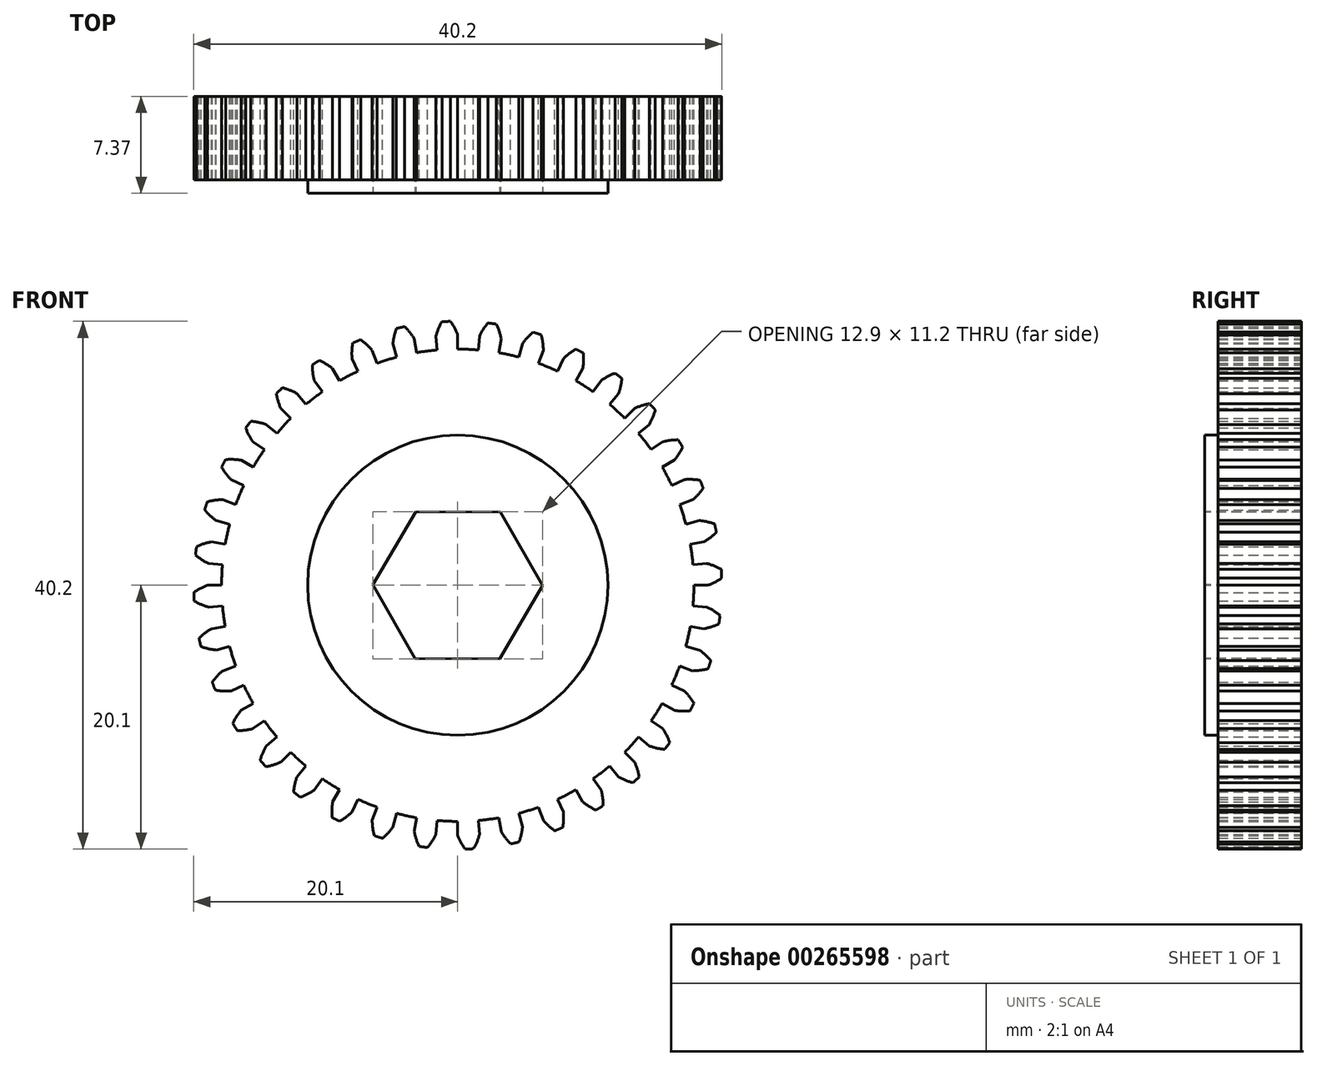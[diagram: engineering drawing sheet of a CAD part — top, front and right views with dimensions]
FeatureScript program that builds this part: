
annotation { "Feature Type Name" : "Feature", "Feature Type Description" : "" }
export const myFeature = defineFeature(function(context is Context, id is Id, definition is map)
    precondition{}
    {
        {
            var Q0;
            Q0=qCreatedBy(makeId("Front.planeOp"),FACE);
            var sketch = newSketch(context, id + "F0", { "sketchPlane" : qUnion([Q0])});
            skArc(sketch, "E0", {"start": v(-1.57, 17.91) * mm, "mid": v(-2.35, 17.83) * mm, "end": v(-3.12, 17.7) * mm});
            skArc(sketch, "E1", {"start": v(-0.55, 20.1) * mm, "mid": v(-0.71, 20.1) * mm, "end": v(-0.88, 20.08) * mm});
            skPoint(sketch, "E2.endSnap0", {"position": v(-1.68, 19.21) * mm});
            skArc(sketch, "E3.trimOffspring", {"start": v(0, 19.05) * mm, "mid": v(-0.24, 19.6) * mm, "end": v(-0.55, 20.1) * mm});
            skLineSegment(sketch, "E4.trimOffspring", {"start": v(0, 17.93) * mm, "end": v(0, 19.05) * mm});
            skLineSegment(sketch, "E5.MirrorCS", {"start": v(-1.56, 17.86) * mm, "end": v(-1.66, 18.98) * mm});
            skArc(sketch, "E6.MirrorCS", {"start": v(-1.66, 18.98) * mm, "mid": v(-1.47, 19.54) * mm, "end": v(-1.2, 20.07) * mm});
            skArc(sketch, "E7.MirrorCS", {"start": v(-1.2, 20.07) * mm, "mid": v(-1.04, 20.08) * mm, "end": v(-0.88, 20.08) * mm});
            skArc(sketch, "E8.1.0", {"start": v(-4.67, 19.55) * mm, "mid": v(-4.51, 19.6) * mm, "end": v(-4.35, 19.63) * mm});
            skArc(sketch, "E8.1.1", {"start": v(-4.93, 18.4) * mm, "mid": v(-4.84, 18.99) * mm, "end": v(-4.67, 19.55) * mm});
            skLineSegment(sketch, "E8.1.2", {"start": v(-4.64, 17.32) * mm, "end": v(-4.93, 18.4) * mm});
            skArc(sketch, "E8.1.3", {"start": v(-4.03, 19.7) * mm, "mid": v(-4.2, 19.66) * mm, "end": v(-4.35, 19.63) * mm});
            skArc(sketch, "E8.1.4", {"start": v(-3.3, 18.76) * mm, "mid": v(-3.64, 19.25) * mm, "end": v(-4.03, 19.7) * mm});
            skLineSegment(sketch, "E8.1.5", {"start": v(-3.11, 17.66) * mm, "end": v(-3.3, 18.76) * mm});
            skArc(sketch, "E8.2.0", {"start": v(-8, 18.45) * mm, "mid": v(-7.84, 18.51) * mm, "end": v(-7.7, 18.57) * mm});
            skArc(sketch, "E8.2.1", {"start": v(-8.05, 17.27) * mm, "mid": v(-8.06, 17.86) * mm, "end": v(-8, 18.45) * mm});
            skLineSegment(sketch, "E8.2.2", {"start": v(-7.58, 16.25) * mm, "end": v(-8.05, 17.27) * mm});
            skArc(sketch, "E8.2.3", {"start": v(-7.4, 18.7) * mm, "mid": v(-7.54, 18.64) * mm, "end": v(-7.7, 18.57) * mm});
            skArc(sketch, "E8.2.4", {"start": v(-6.52, 17.9) * mm, "mid": v(-6.93, 18.33) * mm, "end": v(-7.4, 18.7) * mm});
            skLineSegment(sketch, "E8.2.5", {"start": v(-6.13, 16.85) * mm, "end": v(-6.52, 17.9) * mm});
            skArc(sketch, "E8.3.0", {"start": v(-11.08, 16.78) * mm, "mid": v(-10.94, 16.87) * mm, "end": v(-10.8, 16.96) * mm});
            skArc(sketch, "E8.3.1", {"start": v(-10.93, 15.6) * mm, "mid": v(-11.04, 16.19) * mm, "end": v(-11.08, 16.78) * mm});
            skLineSegment(sketch, "E8.3.2", {"start": v(-10.29, 14.69) * mm, "end": v(-10.93, 15.6) * mm});
            skArc(sketch, "E8.3.3", {"start": v(-10.53, 17.13) * mm, "mid": v(-10.66, 17.04) * mm, "end": v(-10.8, 16.96) * mm});
            skArc(sketch, "E8.3.4", {"start": v(-9.52, 16.5) * mm, "mid": v(-10, 16.84) * mm, "end": v(-10.53, 17.13) * mm});
            skLineSegment(sketch, "E8.3.5", {"start": v(-8.97, 15.53) * mm, "end": v(-9.52, 16.5) * mm});
            skArc(sketch, "E8.4.0", {"start": v(-13.82, 14.6) * mm, "mid": v(-13.7, 14.71) * mm, "end": v(-13.58, 14.82) * mm});
            skArc(sketch, "E8.4.1", {"start": v(-13.47, 13.47) * mm, "mid": v(-13.68, 14.02) * mm, "end": v(-13.82, 14.6) * mm});
            skLineSegment(sketch, "E8.4.2", {"start": v(-12.68, 12.68) * mm, "end": v(-13.47, 13.47) * mm});
            skArc(sketch, "E8.4.3", {"start": v(-13.34, 15.04) * mm, "mid": v(-13.46, 14.93) * mm, "end": v(-13.58, 14.82) * mm});
            skArc(sketch, "E8.4.4", {"start": v(-12.25, 14.6) * mm, "mid": v(-12.78, 14.85) * mm, "end": v(-13.34, 15.04) * mm});
            skLineSegment(sketch, "E8.4.5", {"start": v(-11.53, 13.74) * mm, "end": v(-12.25, 14.6) * mm});
            skArc(sketch, "E8.5.0", {"start": v(-16.15, 11.98) * mm, "mid": v(-16.05, 12.1) * mm, "end": v(-15.95, 12.24) * mm});
            skArc(sketch, "E8.5.1", {"start": v(-15.6, 10.93) * mm, "mid": v(-15.9, 11.44) * mm, "end": v(-16.15, 11.98) * mm});
            skLineSegment(sketch, "E8.5.2", {"start": v(-14.69, 10.29) * mm, "end": v(-15.6, 10.93) * mm});
            skArc(sketch, "E8.5.3", {"start": v(-15.75, 12.5) * mm, "mid": v(-15.85, 12.37) * mm, "end": v(-15.95, 12.24) * mm});
            skArc(sketch, "E8.5.4", {"start": v(-14.6, 12.25) * mm, "mid": v(-15.16, 12.4) * mm, "end": v(-15.75, 12.5) * mm});
            skLineSegment(sketch, "E8.5.5", {"start": v(-13.74, 11.53) * mm, "end": v(-14.6, 12.25) * mm});
            skArc(sketch, "E8.6.0", {"start": v(-17.98, 9) * mm, "mid": v(-17.9, 9.14) * mm, "end": v(-17.83, 9.28) * mm});
            skArc(sketch, "E8.6.1", {"start": v(-17.27, 8.05) * mm, "mid": v(-17.65, 8.5) * mm, "end": v(-17.98, 9) * mm});
            skLineSegment(sketch, "E8.6.2", {"start": v(-16.25, 7.58) * mm, "end": v(-17.27, 8.05) * mm});
            skArc(sketch, "E8.6.3", {"start": v(-17.68, 9.57) * mm, "mid": v(-17.76, 9.43) * mm, "end": v(-17.83, 9.28) * mm});
            skArc(sketch, "E8.6.4", {"start": v(-16.5, 9.53) * mm, "mid": v(-17.09, 9.58) * mm, "end": v(-17.68, 9.57) * mm});
            skLineSegment(sketch, "E8.6.5", {"start": v(-15.53, 8.97) * mm, "end": v(-16.5, 9.53) * mm});
            skArc(sketch, "E8.7.0", {"start": v(-19.27, 5.73) * mm, "mid": v(-19.22, 5.89) * mm, "end": v(-19.17, 6.05) * mm});
            skArc(sketch, "E8.7.1", {"start": v(-18.4, 4.93) * mm, "mid": v(-18.86, 5.3) * mm, "end": v(-19.27, 5.73) * mm});
            skLineSegment(sketch, "E8.7.2", {"start": v(-17.32, 4.64) * mm, "end": v(-18.4, 4.93) * mm});
            skArc(sketch, "E8.7.3", {"start": v(-19.07, 6.36) * mm, "mid": v(-19.12, 6.2) * mm, "end": v(-19.17, 6.05) * mm});
            skArc(sketch, "E8.7.4", {"start": v(-17.9, 6.52) * mm, "mid": v(-18.5, 6.47) * mm, "end": v(-19.07, 6.36) * mm});
            skLineSegment(sketch, "E8.7.5", {"start": v(-16.85, 6.13) * mm, "end": v(-17.9, 6.52) * mm});
            skArc(sketch, "E8.8.0", {"start": v(-19.97, 2.3) * mm, "mid": v(-19.95, 2.46) * mm, "end": v(-19.93, 2.62) * mm});
            skArc(sketch, "E8.8.1", {"start": v(-18.98, 1.66) * mm, "mid": v(-19.5, 1.95) * mm, "end": v(-19.97, 2.3) * mm});
            skLineSegment(sketch, "E8.8.2", {"start": v(-17.86, 1.56) * mm, "end": v(-18.98, 1.66) * mm});
            skArc(sketch, "E8.8.3", {"start": v(-19.89, 2.95) * mm, "mid": v(-19.91, 2.79) * mm, "end": v(-19.93, 2.62) * mm});
            skArc(sketch, "E8.8.4", {"start": v(-18.76, 3.3) * mm, "mid": v(-19.34, 3.16) * mm, "end": v(-19.89, 2.95) * mm});
            skLineSegment(sketch, "E8.8.5", {"start": v(-17.66, 3.11) * mm, "end": v(-18.76, 3.3) * mm});
            skArc(sketch, "E8.9.0", {"start": v(-20.07, -1.2) * mm, "mid": v(-20.08, -1.04) * mm, "end": v(-20.08, -0.88) * mm});
            skArc(sketch, "E8.9.1", {"start": v(-18.98, -1.66) * mm, "mid": v(-19.54, -1.47) * mm, "end": v(-20.07, -1.2) * mm});
            skLineSegment(sketch, "E8.9.2", {"start": v(-17.86, -1.56) * mm, "end": v(-18.98, -1.66) * mm});
            skArc(sketch, "E8.9.3", {"start": v(-20.1, -0.55) * mm, "mid": v(-20.1, -0.71) * mm, "end": v(-20.08, -0.88) * mm});
            skArc(sketch, "E8.9.4", {"start": v(-19.05, 0) * mm, "mid": v(-19.6, -0.24) * mm, "end": v(-20.1, -0.55) * mm});
            skLineSegment(sketch, "E8.9.5", {"start": v(-17.93, 0) * mm, "end": v(-19.05, 0) * mm});
            skArc(sketch, "E8.10.0", {"start": v(-19.55, -4.67) * mm, "mid": v(-19.6, -4.51) * mm, "end": v(-19.63, -4.35) * mm});
            skArc(sketch, "E8.10.1", {"start": v(-18.4, -4.93) * mm, "mid": v(-18.99, -4.84) * mm, "end": v(-19.55, -4.67) * mm});
            skLineSegment(sketch, "E8.10.2", {"start": v(-17.32, -4.64) * mm, "end": v(-18.4, -4.93) * mm});
            skArc(sketch, "E8.10.3", {"start": v(-19.7, -4.03) * mm, "mid": v(-19.66, -4.2) * mm, "end": v(-19.63, -4.35) * mm});
            skArc(sketch, "E8.10.4", {"start": v(-18.76, -3.3) * mm, "mid": v(-19.25, -3.64) * mm, "end": v(-19.7, -4.03) * mm});
            skLineSegment(sketch, "E8.10.5", {"start": v(-17.66, -3.11) * mm, "end": v(-18.76, -3.3) * mm});
            skArc(sketch, "E8.11.0", {"start": v(-18.45, -8) * mm, "mid": v(-18.51, -7.84) * mm, "end": v(-18.57, -7.7) * mm});
            skArc(sketch, "E8.11.1", {"start": v(-17.27, -8.05) * mm, "mid": v(-17.86, -8.06) * mm, "end": v(-18.45, -8) * mm});
            skLineSegment(sketch, "E8.11.2", {"start": v(-16.25, -7.58) * mm, "end": v(-17.27, -8.05) * mm});
            skArc(sketch, "E8.11.3", {"start": v(-18.7, -7.4) * mm, "mid": v(-18.64, -7.54) * mm, "end": v(-18.57, -7.7) * mm});
            skArc(sketch, "E8.11.4", {"start": v(-17.9, -6.52) * mm, "mid": v(-18.33, -6.93) * mm, "end": v(-18.7, -7.4) * mm});
            skLineSegment(sketch, "E8.11.5", {"start": v(-16.85, -6.13) * mm, "end": v(-17.9, -6.52) * mm});
            skArc(sketch, "E8.12.0", {"start": v(-16.78, -11.08) * mm, "mid": v(-16.87, -10.94) * mm, "end": v(-16.96, -10.8) * mm});
            skArc(sketch, "E8.12.1", {"start": v(-15.6, -10.93) * mm, "mid": v(-16.19, -11.04) * mm, "end": v(-16.78, -11.08) * mm});
            skLineSegment(sketch, "E8.12.2", {"start": v(-14.69, -10.29) * mm, "end": v(-15.6, -10.93) * mm});
            skArc(sketch, "E8.12.3", {"start": v(-17.13, -10.53) * mm, "mid": v(-17.04, -10.66) * mm, "end": v(-16.96, -10.8) * mm});
            skArc(sketch, "E8.12.4", {"start": v(-16.5, -9.52) * mm, "mid": v(-16.84, -10) * mm, "end": v(-17.13, -10.53) * mm});
            skLineSegment(sketch, "E8.12.5", {"start": v(-15.53, -8.97) * mm, "end": v(-16.5, -9.52) * mm});
            skArc(sketch, "E8.13.0", {"start": v(-14.6, -13.82) * mm, "mid": v(-14.71, -13.7) * mm, "end": v(-14.82, -13.58) * mm});
            skArc(sketch, "E8.13.1", {"start": v(-13.47, -13.47) * mm, "mid": v(-14.02, -13.68) * mm, "end": v(-14.6, -13.82) * mm});
            skLineSegment(sketch, "E8.13.2", {"start": v(-12.68, -12.68) * mm, "end": v(-13.47, -13.47) * mm});
            skArc(sketch, "E8.13.3", {"start": v(-15.04, -13.34) * mm, "mid": v(-14.93, -13.46) * mm, "end": v(-14.82, -13.58) * mm});
            skArc(sketch, "E8.13.4", {"start": v(-14.6, -12.25) * mm, "mid": v(-14.85, -12.78) * mm, "end": v(-15.04, -13.34) * mm});
            skLineSegment(sketch, "E8.13.5", {"start": v(-13.74, -11.53) * mm, "end": v(-14.6, -12.25) * mm});
            skArc(sketch, "E8.14.0", {"start": v(-11.98, -16.15) * mm, "mid": v(-12.1, -16.05) * mm, "end": v(-12.24, -15.95) * mm});
            skArc(sketch, "E8.14.1", {"start": v(-10.93, -15.6) * mm, "mid": v(-11.44, -15.9) * mm, "end": v(-11.98, -16.15) * mm});
            skLineSegment(sketch, "E8.14.2", {"start": v(-10.29, -14.69) * mm, "end": v(-10.93, -15.6) * mm});
            skArc(sketch, "E8.14.3", {"start": v(-12.5, -15.75) * mm, "mid": v(-12.37, -15.85) * mm, "end": v(-12.24, -15.95) * mm});
            skArc(sketch, "E8.14.4", {"start": v(-12.25, -14.6) * mm, "mid": v(-12.4, -15.16) * mm, "end": v(-12.5, -15.75) * mm});
            skLineSegment(sketch, "E8.14.5", {"start": v(-11.53, -13.74) * mm, "end": v(-12.25, -14.6) * mm});
            skArc(sketch, "E8.15.0", {"start": v(-9, -17.98) * mm, "mid": v(-9.14, -17.9) * mm, "end": v(-9.28, -17.83) * mm});
            skArc(sketch, "E8.15.1", {"start": v(-8.05, -17.27) * mm, "mid": v(-8.5, -17.65) * mm, "end": v(-9, -17.98) * mm});
            skLineSegment(sketch, "E8.15.2", {"start": v(-7.58, -16.25) * mm, "end": v(-8.05, -17.27) * mm});
            skArc(sketch, "E8.15.3", {"start": v(-9.57, -17.68) * mm, "mid": v(-9.43, -17.76) * mm, "end": v(-9.28, -17.83) * mm});
            skArc(sketch, "E8.15.4", {"start": v(-9.53, -16.5) * mm, "mid": v(-9.58, -17.09) * mm, "end": v(-9.57, -17.68) * mm});
            skLineSegment(sketch, "E8.15.5", {"start": v(-8.97, -15.53) * mm, "end": v(-9.53, -16.5) * mm});
            skArc(sketch, "E8.16.0", {"start": v(-5.73, -19.27) * mm, "mid": v(-5.89, -19.22) * mm, "end": v(-6.05, -19.17) * mm});
            skArc(sketch, "E8.16.1", {"start": v(-4.93, -18.4) * mm, "mid": v(-5.3, -18.86) * mm, "end": v(-5.73, -19.27) * mm});
            skLineSegment(sketch, "E8.16.2", {"start": v(-4.64, -17.32) * mm, "end": v(-4.93, -18.4) * mm});
            skArc(sketch, "E8.16.3", {"start": v(-6.36, -19.07) * mm, "mid": v(-6.2, -19.12) * mm, "end": v(-6.05, -19.17) * mm});
            skArc(sketch, "E8.16.4", {"start": v(-6.52, -17.9) * mm, "mid": v(-6.47, -18.5) * mm, "end": v(-6.36, -19.07) * mm});
            skLineSegment(sketch, "E8.16.5", {"start": v(-6.13, -16.85) * mm, "end": v(-6.52, -17.9) * mm});
            skArc(sketch, "E8.17.0", {"start": v(-2.3, -19.97) * mm, "mid": v(-2.46, -19.95) * mm, "end": v(-2.62, -19.93) * mm});
            skArc(sketch, "E8.17.1", {"start": v(-1.66, -18.98) * mm, "mid": v(-1.95, -19.5) * mm, "end": v(-2.3, -19.97) * mm});
            skLineSegment(sketch, "E8.17.2", {"start": v(-1.56, -17.86) * mm, "end": v(-1.66, -18.98) * mm});
            skArc(sketch, "E8.17.3", {"start": v(-2.95, -19.89) * mm, "mid": v(-2.79, -19.91) * mm, "end": v(-2.62, -19.93) * mm});
            skArc(sketch, "E8.17.4", {"start": v(-3.3, -18.76) * mm, "mid": v(-3.16, -19.34) * mm, "end": v(-2.95, -19.89) * mm});
            skLineSegment(sketch, "E8.17.5", {"start": v(-3.11, -17.66) * mm, "end": v(-3.3, -18.76) * mm});
            skArc(sketch, "E8.18.0", {"start": v(1.2, -20.07) * mm, "mid": v(1.04, -20.08) * mm, "end": v(0.88, -20.08) * mm});
            skArc(sketch, "E8.18.1", {"start": v(1.66, -18.98) * mm, "mid": v(1.47, -19.54) * mm, "end": v(1.2, -20.07) * mm});
            skLineSegment(sketch, "E8.18.2", {"start": v(1.56, -17.86) * mm, "end": v(1.66, -18.98) * mm});
            skArc(sketch, "E8.18.3", {"start": v(0.55, -20.1) * mm, "mid": v(0.71, -20.1) * mm, "end": v(0.88, -20.08) * mm});
            skArc(sketch, "E8.18.4", {"start": v(0, -19.05) * mm, "mid": v(0.24, -19.6) * mm, "end": v(0.55, -20.1) * mm});
            skLineSegment(sketch, "E8.18.5", {"start": v(0, -17.93) * mm, "end": v(0, -19.05) * mm});
            skArc(sketch, "E8.19.0", {"start": v(4.67, -19.55) * mm, "mid": v(4.51, -19.6) * mm, "end": v(4.35, -19.63) * mm});
            skArc(sketch, "E8.19.1", {"start": v(4.93, -18.4) * mm, "mid": v(4.84, -18.99) * mm, "end": v(4.67, -19.55) * mm});
            skLineSegment(sketch, "E8.19.2", {"start": v(4.64, -17.32) * mm, "end": v(4.93, -18.4) * mm});
            skArc(sketch, "E8.19.3", {"start": v(4.03, -19.7) * mm, "mid": v(4.2, -19.66) * mm, "end": v(4.35, -19.63) * mm});
            skArc(sketch, "E8.19.4", {"start": v(3.3, -18.76) * mm, "mid": v(3.64, -19.25) * mm, "end": v(4.03, -19.7) * mm});
            skLineSegment(sketch, "E8.19.5", {"start": v(3.11, -17.66) * mm, "end": v(3.3, -18.76) * mm});
            skArc(sketch, "E8.20.0", {"start": v(8, -18.45) * mm, "mid": v(7.84, -18.51) * mm, "end": v(7.7, -18.57) * mm});
            skArc(sketch, "E8.20.1", {"start": v(8.05, -17.27) * mm, "mid": v(8.06, -17.86) * mm, "end": v(8, -18.45) * mm});
            skLineSegment(sketch, "E8.20.2", {"start": v(7.58, -16.25) * mm, "end": v(8.05, -17.27) * mm});
            skArc(sketch, "E8.20.3", {"start": v(7.4, -18.7) * mm, "mid": v(7.54, -18.64) * mm, "end": v(7.7, -18.57) * mm});
            skArc(sketch, "E8.20.4", {"start": v(6.52, -17.9) * mm, "mid": v(6.93, -18.33) * mm, "end": v(7.4, -18.7) * mm});
            skLineSegment(sketch, "E8.20.5", {"start": v(6.13, -16.85) * mm, "end": v(6.52, -17.9) * mm});
            skArc(sketch, "E8.21.0", {"start": v(11.08, -16.78) * mm, "mid": v(10.94, -16.87) * mm, "end": v(10.8, -16.96) * mm});
            skArc(sketch, "E8.21.1", {"start": v(10.93, -15.6) * mm, "mid": v(11.04, -16.19) * mm, "end": v(11.08, -16.78) * mm});
            skLineSegment(sketch, "E8.21.2", {"start": v(10.29, -14.69) * mm, "end": v(10.93, -15.6) * mm});
            skArc(sketch, "E8.21.3", {"start": v(10.53, -17.13) * mm, "mid": v(10.66, -17.04) * mm, "end": v(10.8, -16.96) * mm});
            skArc(sketch, "E8.21.4", {"start": v(9.53, -16.5) * mm, "mid": v(10, -16.84) * mm, "end": v(10.53, -17.13) * mm});
            skLineSegment(sketch, "E8.21.5", {"start": v(8.97, -15.53) * mm, "end": v(9.53, -16.5) * mm});
            skArc(sketch, "E8.22.0", {"start": v(13.82, -14.6) * mm, "mid": v(13.7, -14.71) * mm, "end": v(13.58, -14.82) * mm});
            skArc(sketch, "E8.22.1", {"start": v(13.47, -13.47) * mm, "mid": v(13.68, -14.02) * mm, "end": v(13.82, -14.6) * mm});
            skLineSegment(sketch, "E8.22.2", {"start": v(12.68, -12.68) * mm, "end": v(13.47, -13.47) * mm});
            skArc(sketch, "E8.22.3", {"start": v(13.34, -15.04) * mm, "mid": v(13.46, -14.93) * mm, "end": v(13.58, -14.82) * mm});
            skArc(sketch, "E8.22.4", {"start": v(12.25, -14.6) * mm, "mid": v(12.78, -14.85) * mm, "end": v(13.34, -15.04) * mm});
            skLineSegment(sketch, "E8.22.5", {"start": v(11.53, -13.74) * mm, "end": v(12.25, -14.6) * mm});
            skArc(sketch, "E8.23.0", {"start": v(16.15, -11.98) * mm, "mid": v(16.05, -12.1) * mm, "end": v(15.95, -12.24) * mm});
            skArc(sketch, "E8.23.1", {"start": v(15.6, -10.93) * mm, "mid": v(15.9, -11.44) * mm, "end": v(16.15, -11.98) * mm});
            skLineSegment(sketch, "E8.23.2", {"start": v(14.69, -10.29) * mm, "end": v(15.6, -10.93) * mm});
            skArc(sketch, "E8.23.3", {"start": v(15.75, -12.5) * mm, "mid": v(15.85, -12.37) * mm, "end": v(15.95, -12.24) * mm});
            skArc(sketch, "E8.23.4", {"start": v(14.6, -12.25) * mm, "mid": v(15.16, -12.4) * mm, "end": v(15.75, -12.5) * mm});
            skLineSegment(sketch, "E8.23.5", {"start": v(13.74, -11.53) * mm, "end": v(14.6, -12.25) * mm});
            skArc(sketch, "E8.24.0", {"start": v(17.98, -9) * mm, "mid": v(17.9, -9.14) * mm, "end": v(17.83, -9.28) * mm});
            skArc(sketch, "E8.24.1", {"start": v(17.27, -8.05) * mm, "mid": v(17.65, -8.5) * mm, "end": v(17.98, -9) * mm});
            skLineSegment(sketch, "E8.24.2", {"start": v(16.25, -7.58) * mm, "end": v(17.27, -8.05) * mm});
            skArc(sketch, "E8.24.3", {"start": v(17.68, -9.57) * mm, "mid": v(17.76, -9.43) * mm, "end": v(17.83, -9.28) * mm});
            skArc(sketch, "E8.24.4", {"start": v(16.5, -9.53) * mm, "mid": v(17.09, -9.58) * mm, "end": v(17.68, -9.57) * mm});
            skLineSegment(sketch, "E8.24.5", {"start": v(15.53, -8.97) * mm, "end": v(16.5, -9.53) * mm});
            skArc(sketch, "E8.25.0", {"start": v(19.27, -5.73) * mm, "mid": v(19.22, -5.89) * mm, "end": v(19.17, -6.05) * mm});
            skArc(sketch, "E8.25.1", {"start": v(18.4, -4.93) * mm, "mid": v(18.86, -5.3) * mm, "end": v(19.27, -5.73) * mm});
            skLineSegment(sketch, "E8.25.2", {"start": v(17.32, -4.64) * mm, "end": v(18.4, -4.93) * mm});
            skArc(sketch, "E8.25.3", {"start": v(19.07, -6.36) * mm, "mid": v(19.12, -6.2) * mm, "end": v(19.17, -6.05) * mm});
            skArc(sketch, "E8.25.4", {"start": v(17.9, -6.52) * mm, "mid": v(18.5, -6.47) * mm, "end": v(19.07, -6.36) * mm});
            skLineSegment(sketch, "E8.25.5", {"start": v(16.85, -6.13) * mm, "end": v(17.9, -6.52) * mm});
            skArc(sketch, "E8.26.0", {"start": v(19.97, -2.3) * mm, "mid": v(19.95, -2.46) * mm, "end": v(19.93, -2.62) * mm});
            skArc(sketch, "E8.26.1", {"start": v(18.98, -1.66) * mm, "mid": v(19.5, -1.95) * mm, "end": v(19.97, -2.3) * mm});
            skLineSegment(sketch, "E8.26.2", {"start": v(17.86, -1.56) * mm, "end": v(18.98, -1.66) * mm});
            skArc(sketch, "E8.26.3", {"start": v(19.89, -2.95) * mm, "mid": v(19.91, -2.79) * mm, "end": v(19.93, -2.62) * mm});
            skArc(sketch, "E8.26.4", {"start": v(18.76, -3.3) * mm, "mid": v(19.34, -3.16) * mm, "end": v(19.89, -2.95) * mm});
            skLineSegment(sketch, "E8.26.5", {"start": v(17.66, -3.11) * mm, "end": v(18.76, -3.3) * mm});
            skArc(sketch, "E8.27.0", {"start": v(20.07, 1.2) * mm, "mid": v(20.08, 1.04) * mm, "end": v(20.08, 0.88) * mm});
            skArc(sketch, "E8.27.1", {"start": v(18.98, 1.66) * mm, "mid": v(19.54, 1.47) * mm, "end": v(20.07, 1.2) * mm});
            skLineSegment(sketch, "E8.27.2", {"start": v(17.86, 1.56) * mm, "end": v(18.98, 1.66) * mm});
            skArc(sketch, "E8.27.3", {"start": v(20.1, 0.55) * mm, "mid": v(20.1, 0.71) * mm, "end": v(20.08, 0.88) * mm});
            skArc(sketch, "E8.27.4", {"start": v(19.05, 0) * mm, "mid": v(19.6, 0.24) * mm, "end": v(20.1, 0.55) * mm});
            skLineSegment(sketch, "E8.27.5", {"start": v(17.93, 0) * mm, "end": v(19.05, 0) * mm});
            skArc(sketch, "E8.28.0", {"start": v(19.55, 4.67) * mm, "mid": v(19.6, 4.51) * mm, "end": v(19.63, 4.35) * mm});
            skArc(sketch, "E8.28.1", {"start": v(18.4, 4.93) * mm, "mid": v(18.99, 4.84) * mm, "end": v(19.55, 4.67) * mm});
            skLineSegment(sketch, "E8.28.2", {"start": v(17.32, 4.64) * mm, "end": v(18.4, 4.93) * mm});
            skArc(sketch, "E8.28.3", {"start": v(19.7, 4.03) * mm, "mid": v(19.66, 4.2) * mm, "end": v(19.63, 4.35) * mm});
            skArc(sketch, "E8.28.4", {"start": v(18.76, 3.3) * mm, "mid": v(19.25, 3.64) * mm, "end": v(19.7, 4.03) * mm});
            skLineSegment(sketch, "E8.28.5", {"start": v(17.66, 3.11) * mm, "end": v(18.76, 3.3) * mm});
            skArc(sketch, "E8.29.0", {"start": v(18.45, 8) * mm, "mid": v(18.51, 7.84) * mm, "end": v(18.57, 7.7) * mm});
            skArc(sketch, "E8.29.1", {"start": v(17.27, 8.05) * mm, "mid": v(17.86, 8.06) * mm, "end": v(18.45, 8) * mm});
            skLineSegment(sketch, "E8.29.2", {"start": v(16.25, 7.58) * mm, "end": v(17.27, 8.05) * mm});
            skArc(sketch, "E8.29.3", {"start": v(18.7, 7.4) * mm, "mid": v(18.64, 7.54) * mm, "end": v(18.57, 7.7) * mm});
            skArc(sketch, "E8.29.4", {"start": v(17.9, 6.52) * mm, "mid": v(18.33, 6.93) * mm, "end": v(18.7, 7.4) * mm});
            skLineSegment(sketch, "E8.29.5", {"start": v(16.85, 6.13) * mm, "end": v(17.9, 6.52) * mm});
            skArc(sketch, "E8.30.0", {"start": v(16.78, 11.08) * mm, "mid": v(16.87, 10.94) * mm, "end": v(16.96, 10.8) * mm});
            skArc(sketch, "E8.30.1", {"start": v(15.6, 10.93) * mm, "mid": v(16.19, 11.04) * mm, "end": v(16.78, 11.08) * mm});
            skLineSegment(sketch, "E8.30.2", {"start": v(14.69, 10.29) * mm, "end": v(15.6, 10.93) * mm});
            skArc(sketch, "E8.30.3", {"start": v(17.13, 10.53) * mm, "mid": v(17.04, 10.66) * mm, "end": v(16.96, 10.8) * mm});
            skArc(sketch, "E8.30.4", {"start": v(16.5, 9.52) * mm, "mid": v(16.84, 10) * mm, "end": v(17.13, 10.53) * mm});
            skLineSegment(sketch, "E8.30.5", {"start": v(15.53, 8.97) * mm, "end": v(16.5, 9.52) * mm});
            skArc(sketch, "E8.31.0", {"start": v(14.6, 13.82) * mm, "mid": v(14.71, 13.7) * mm, "end": v(14.82, 13.58) * mm});
            skArc(sketch, "E8.31.1", {"start": v(13.47, 13.47) * mm, "mid": v(14.02, 13.68) * mm, "end": v(14.6, 13.82) * mm});
            skLineSegment(sketch, "E8.31.2", {"start": v(12.68, 12.68) * mm, "end": v(13.47, 13.47) * mm});
            skArc(sketch, "E8.31.3", {"start": v(15.04, 13.34) * mm, "mid": v(14.93, 13.46) * mm, "end": v(14.82, 13.58) * mm});
            skArc(sketch, "E8.31.4", {"start": v(14.6, 12.25) * mm, "mid": v(14.85, 12.78) * mm, "end": v(15.04, 13.34) * mm});
            skLineSegment(sketch, "E8.31.5", {"start": v(13.74, 11.53) * mm, "end": v(14.6, 12.25) * mm});
            skArc(sketch, "E8.32.0", {"start": v(11.98, 16.15) * mm, "mid": v(12.1, 16.05) * mm, "end": v(12.24, 15.95) * mm});
            skArc(sketch, "E8.32.1", {"start": v(10.93, 15.6) * mm, "mid": v(11.44, 15.9) * mm, "end": v(11.98, 16.15) * mm});
            skLineSegment(sketch, "E8.32.2", {"start": v(10.29, 14.69) * mm, "end": v(10.93, 15.6) * mm});
            skArc(sketch, "E8.32.3", {"start": v(12.5, 15.75) * mm, "mid": v(12.37, 15.85) * mm, "end": v(12.24, 15.95) * mm});
            skArc(sketch, "E8.32.4", {"start": v(12.25, 14.6) * mm, "mid": v(12.4, 15.16) * mm, "end": v(12.5, 15.75) * mm});
            skLineSegment(sketch, "E8.32.5", {"start": v(11.53, 13.74) * mm, "end": v(12.25, 14.6) * mm});
            skArc(sketch, "E8.33.0", {"start": v(9, 17.98) * mm, "mid": v(9.14, 17.9) * mm, "end": v(9.28, 17.83) * mm});
            skArc(sketch, "E8.33.1", {"start": v(8.05, 17.27) * mm, "mid": v(8.5, 17.65) * mm, "end": v(9, 17.98) * mm});
            skLineSegment(sketch, "E8.33.2", {"start": v(7.58, 16.25) * mm, "end": v(8.05, 17.27) * mm});
            skArc(sketch, "E8.33.3", {"start": v(9.57, 17.68) * mm, "mid": v(9.43, 17.76) * mm, "end": v(9.28, 17.83) * mm});
            skArc(sketch, "E8.33.4", {"start": v(9.52, 16.5) * mm, "mid": v(9.58, 17.09) * mm, "end": v(9.57, 17.68) * mm});
            skLineSegment(sketch, "E8.33.5", {"start": v(8.97, 15.53) * mm, "end": v(9.52, 16.5) * mm});
            skArc(sketch, "E8.34.0", {"start": v(5.73, 19.27) * mm, "mid": v(5.89, 19.22) * mm, "end": v(6.05, 19.17) * mm});
            skArc(sketch, "E8.34.1", {"start": v(4.93, 18.4) * mm, "mid": v(5.3, 18.86) * mm, "end": v(5.73, 19.27) * mm});
            skLineSegment(sketch, "E8.34.2", {"start": v(4.64, 17.32) * mm, "end": v(4.93, 18.4) * mm});
            skArc(sketch, "E8.34.3", {"start": v(6.36, 19.07) * mm, "mid": v(6.2, 19.12) * mm, "end": v(6.05, 19.17) * mm});
            skArc(sketch, "E8.34.4", {"start": v(6.52, 17.9) * mm, "mid": v(6.47, 18.5) * mm, "end": v(6.36, 19.07) * mm});
            skLineSegment(sketch, "E8.34.5", {"start": v(6.13, 16.85) * mm, "end": v(6.52, 17.9) * mm});
            skArc(sketch, "E8.35.0", {"start": v(2.3, 19.97) * mm, "mid": v(2.46, 19.95) * mm, "end": v(2.62, 19.93) * mm});
            skArc(sketch, "E8.35.1", {"start": v(1.66, 18.98) * mm, "mid": v(1.95, 19.5) * mm, "end": v(2.3, 19.97) * mm});
            skLineSegment(sketch, "E8.35.2", {"start": v(1.56, 17.86) * mm, "end": v(1.66, 18.98) * mm});
            skArc(sketch, "E8.35.3", {"start": v(2.95, 19.89) * mm, "mid": v(2.79, 19.91) * mm, "end": v(2.62, 19.93) * mm});
            skArc(sketch, "E8.35.4", {"start": v(3.3, 18.76) * mm, "mid": v(3.16, 19.34) * mm, "end": v(2.95, 19.89) * mm});
            skLineSegment(sketch, "E8.35.5", {"start": v(3.11, 17.66) * mm, "end": v(3.3, 18.76) * mm});
            skArc(sketch, "E9.trimOffspring", {"start": v(1.57, 17.91) * mm, "mid": v(0.78, 17.97) * mm, "end": v(0, 17.98) * mm});
            skArc(sketch, "E10.trimOffspring", {"start": v(-4.65, 17.37) * mm, "mid": v(-5.4, 17.15) * mm, "end": v(-6.15, 16.9) * mm});
            skArc(sketch, "E11.trimOffspring", {"start": v(-7.6, 16.3) * mm, "mid": v(-8.3, 15.95) * mm, "end": v(-9, 15.57) * mm});
            skArc(sketch, "E12.trimOffspring", {"start": v(4.65, 17.37) * mm, "mid": v(3.9, 17.56) * mm, "end": v(3.12, 17.7) * mm});
            skArc(sketch, "E13.trimOffspring", {"start": v(7.6, 16.3) * mm, "mid": v(6.88, 16.61) * mm, "end": v(6.15, 16.9) * mm});
            skArc(sketch, "E14.trimOffspring", {"start": v(10.31, 14.73) * mm, "mid": v(9.66, 15.17) * mm, "end": v(9, 15.57) * mm});
            skArc(sketch, "E15.trimOffspring", {"start": v(12.72, 12.72) * mm, "mid": v(12.15, 13.26) * mm, "end": v(11.56, 13.78) * mm});
            skArc(sketch, "E16.trimOffspring", {"start": v(14.73, 10.31) * mm, "mid": v(14.27, 10.95) * mm, "end": v(13.78, 11.56) * mm});
            skArc(sketch, "E17.trimOffspring", {"start": v(16.3, 7.6) * mm, "mid": v(15.95, 8.3) * mm, "end": v(15.57, 9) * mm});
            skArc(sketch, "E18.trimOffspring", {"start": v(17.37, 4.65) * mm, "mid": v(17.15, 5.4) * mm, "end": v(16.9, 6.15) * mm});
            skArc(sketch, "E19.trimOffspring", {"start": v(17.91, 1.57) * mm, "mid": v(17.83, 2.35) * mm, "end": v(17.7, 3.12) * mm});
            skArc(sketch, "E20.trimOffspring", {"start": v(17.91, -1.57) * mm, "mid": v(17.97, -0.78) * mm, "end": v(17.98, 0) * mm});
            skArc(sketch, "E21.trimOffspring", {"start": v(17.37, -4.65) * mm, "mid": v(17.56, -3.9) * mm, "end": v(17.7, -3.12) * mm});
            skArc(sketch, "E22.trimOffspring", {"start": v(16.3, -7.6) * mm, "mid": v(16.61, -6.88) * mm, "end": v(16.9, -6.15) * mm});
            skArc(sketch, "E23.trimOffspring", {"start": v(14.73, -10.31) * mm, "mid": v(15.17, -9.66) * mm, "end": v(15.57, -9) * mm});
            skArc(sketch, "E24.trimOffspring", {"start": v(12.72, -12.72) * mm, "mid": v(13.26, -12.15) * mm, "end": v(13.78, -11.56) * mm});
            skArc(sketch, "E25.trimOffspring", {"start": v(10.31, -14.73) * mm, "mid": v(10.95, -14.27) * mm, "end": v(11.56, -13.78) * mm});
            skArc(sketch, "E26.trimOffspring", {"start": v(7.6, -16.3) * mm, "mid": v(8.3, -15.95) * mm, "end": v(9, -15.57) * mm});
            skArc(sketch, "E27.trimOffspring", {"start": v(4.65, -17.37) * mm, "mid": v(5.4, -17.15) * mm, "end": v(6.15, -16.9) * mm});
            skArc(sketch, "E28.trimOffspring", {"start": v(1.57, -17.91) * mm, "mid": v(2.35, -17.83) * mm, "end": v(3.12, -17.7) * mm});
            skArc(sketch, "E29.trimOffspring", {"start": v(-1.57, -17.91) * mm, "mid": v(-0.78, -17.97) * mm, "end": v(0, -17.98) * mm});
            skArc(sketch, "E30.trimOffspring", {"start": v(-4.65, -17.37) * mm, "mid": v(-3.9, -17.56) * mm, "end": v(-3.12, -17.7) * mm});
            skArc(sketch, "E31.trimOffspring", {"start": v(-7.6, -16.3) * mm, "mid": v(-6.88, -16.61) * mm, "end": v(-6.15, -16.9) * mm});
            skArc(sketch, "E32.trimOffspring", {"start": v(-10.31, -14.73) * mm, "mid": v(-9.66, -15.17) * mm, "end": v(-9, -15.57) * mm});
            skArc(sketch, "E33.trimOffspring", {"start": v(-12.72, -12.72) * mm, "mid": v(-12.15, -13.26) * mm, "end": v(-11.56, -13.78) * mm});
            skArc(sketch, "E34.trimOffspring", {"start": v(-14.73, -10.31) * mm, "mid": v(-14.27, -10.95) * mm, "end": v(-13.78, -11.56) * mm});
            skArc(sketch, "E35.trimOffspring", {"start": v(-16.3, -7.6) * mm, "mid": v(-15.95, -8.3) * mm, "end": v(-15.57, -9) * mm});
            skArc(sketch, "E36.trimOffspring", {"start": v(-17.37, -4.65) * mm, "mid": v(-17.15, -5.4) * mm, "end": v(-16.9, -6.15) * mm});
            skArc(sketch, "E37.trimOffspring", {"start": v(-17.91, -1.57) * mm, "mid": v(-17.83, -2.35) * mm, "end": v(-17.7, -3.12) * mm});
            skArc(sketch, "E38.trimOffspring", {"start": v(-17.91, 1.57) * mm, "mid": v(-17.97, 0.78) * mm, "end": v(-17.98, 0) * mm});
            skArc(sketch, "E39.trimOffspring", {"start": v(-17.37, 4.65) * mm, "mid": v(-17.56, 3.9) * mm, "end": v(-17.7, 3.12) * mm});
            skArc(sketch, "E40.trimOffspring", {"start": v(-16.3, 7.6) * mm, "mid": v(-16.61, 6.88) * mm, "end": v(-16.9, 6.15) * mm});
            skArc(sketch, "E41.trimOffspring", {"start": v(-14.73, 10.31) * mm, "mid": v(-15.17, 9.66) * mm, "end": v(-15.57, 9) * mm});
            skArc(sketch, "E42.trimOffspring", {"start": v(-12.72, 12.72) * mm, "mid": v(-13.26, 12.15) * mm, "end": v(-13.78, 11.56) * mm});
            skArc(sketch, "E43.trimOffspring", {"start": v(-10.31, 14.73) * mm, "mid": v(-10.95, 14.27) * mm, "end": v(-11.56, 13.78) * mm});
            skSolve(sketch);
        }
        {
            var Q0;
            {var subQ101=sQuery(id+"F0.wireOp",EDGE,"E0");Q0=makeQuery(id+"F0.imprint","IMPRINT",FACE,{"disambiguationData":[TD([[makeQuery(id+"F0.imprint","IMPRINT",EDGE,{"derivedFrom":subQ101}),1.0]])]});}
            extrude(context, id + "F1", {"entities" : qUnion([Q0]), "depth" : 6.35 * mm});
        }
        {
            var Q0;
            Q0=qCreatedBy(makeId("Front.planeOp"),FACE);
            var sketch = newSketch(context, id + "F2", { "sketchPlane" : qUnion([Q0])});
            skCircle(sketch, "E44", {"center": v(0, 0) * mm, "radius": 11.43 * mm});
            skSolve(sketch);
        }
        {
            var Q0;
            Q0 = qSketchRegion(id + "F2", true);
            extrude(context, id + "F3", {"entities" : qUnion([Q0]), "operationType" : NewBodyOperationType.ADD, "depth" : 7.37 * mm});
        }
        {
            var Q0;
            Q0=makeQuery(id+"F3.opExtrude","CAP_FACE",FACE,{"disambiguationData":[OSD([sQuery(id+"F2.wireOp",EDGE,"E44")])],"isStart":false});
            var sketch = newSketch(context, id + "F4", { "sketchPlane" : qUnion([Q0])});
            skCircle(sketch, "E45.cCircle", {"center": v(0, 0) * mm, "radius": 6.45 * mm, "construction": true});
            skLineSegment(sketch, "E45.0", {"start": v(3.25, 5.57) * mm, "end": v(6.45, -0.03) * mm});
            skLineSegment(sketch, "E45.1", {"start": v(6.45, -0.03) * mm, "end": v(3.2, -5.6) * mm});
            skLineSegment(sketch, "E45.2", {"start": v(3.2, -5.6) * mm, "end": v(-3.25, -5.57) * mm});
            skLineSegment(sketch, "E45.3", {"start": v(-3.25, -5.57) * mm, "end": v(-6.45, 0.03) * mm});
            skLineSegment(sketch, "E45.4", {"start": v(-6.45, 0.03) * mm, "end": v(-3.2, 5.6) * mm});
            skLineSegment(sketch, "E45.5", {"start": v(-3.2, 5.6) * mm, "end": v(3.25, 5.57) * mm});
            skSolve(sketch);
        }
        {
            var Q0;
            Q0 = qSketchRegion(id + "F4", true);
            extrude(context, id + "F5", {"entities" : qUnion([Q0]), "operationType" : NewBodyOperationType.REMOVE, "oppositeDirection" : true, "depth" : 254 * mm});
        }
    });
